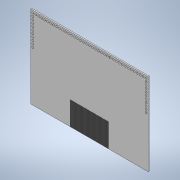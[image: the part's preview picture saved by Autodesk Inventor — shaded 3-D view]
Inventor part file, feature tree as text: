
AUTODESK INVENTOR PART (.ipt)
format: ipt  version: 2021 (Build 250183000, 183)  size: 846,336 bytes
history: native  units: in
note: dims shown in document units (in); Inventor stores cm internally (conversion verified against a paired STEP export)
features: extrude x5, projected_geometry x4, sketch x3, pattern_linear x2, mirror x1
ambient origin geometry x8: Origin, YZ Plane, XZ Plane, XY Plane, X Axis, Y Axis, Z Axis, Center Point
bodies: Solid1 (feature_tree)
feature tree (15):
  extrude  "Extrusion1"  Depth=2.7559in
  extrude  "Extrusion2"  Depth=0.0118in
  pattern_linear  "Rectangular Pattern1"  Count1=2  [1 undecoded]
  extrude  "Extrusion3"  Depth=0.0236in
  pattern_linear  "Rectangular Pattern2"  Count1=4  [1 undecoded]
  extrude  "Extrusion4"  Depth=0.0014in
  extrude  "Extrusion5"  Depth=0.0014in
  mirror  "Mirror1"
  sketch  "Sketch1"  dims[d0=3.937in d1=2.7559in]
  sketch  "Sketch2"  dims[d2=0.0394in d3=0.0in d4=0.0118in d5=0.7874in]
  projected_geometry  "Projected Loop1"
  projected_geometry  "Projected Loop2"
  projected_geometry  "Projected Loop3"
  sketch  "Sketch5"  dims[d6=0.0014in d7=0.0in d8=21.6535in d10=0.0236in d11=1.5748in d12=0.1969in d13=0.0689in d16=0.0014in d17=0.0in d18=0.0787in d19=15.3543in d21=0.1in d22=4.3307in d24=0.1in d25=0.0118in d26=0.0118in d27=0.0118in d28=0.0118in d29=0.0118in d30=0.0118in d31=0.0118in d32=0.0118in d33=0.0118in d34=0.0118in d35=0.0118in d36=0.0118in d37=0.0118in d38=0.0118in d39=0.0118in d40=0.0118in d41=0.0118in d42=0.0118in d43=0.0118in d44=0.0118in d45=0.0118in d46=0.0118in d47=0.0118in d48=0.0118in d49=0.0118in d50=0.0118in d51=0.0118in d52=0.0118in d53=0.0014in d54=0.0in d55=0.0295in d56=0.0in d57=0.0in]
  projected_geometry  "Projected Loop4"
note: 2 required parameter values undecoded (feature->parameter linkage not recoverable at this tier; creation-order binding heuristic only, values carry confidence <= 0.55)
